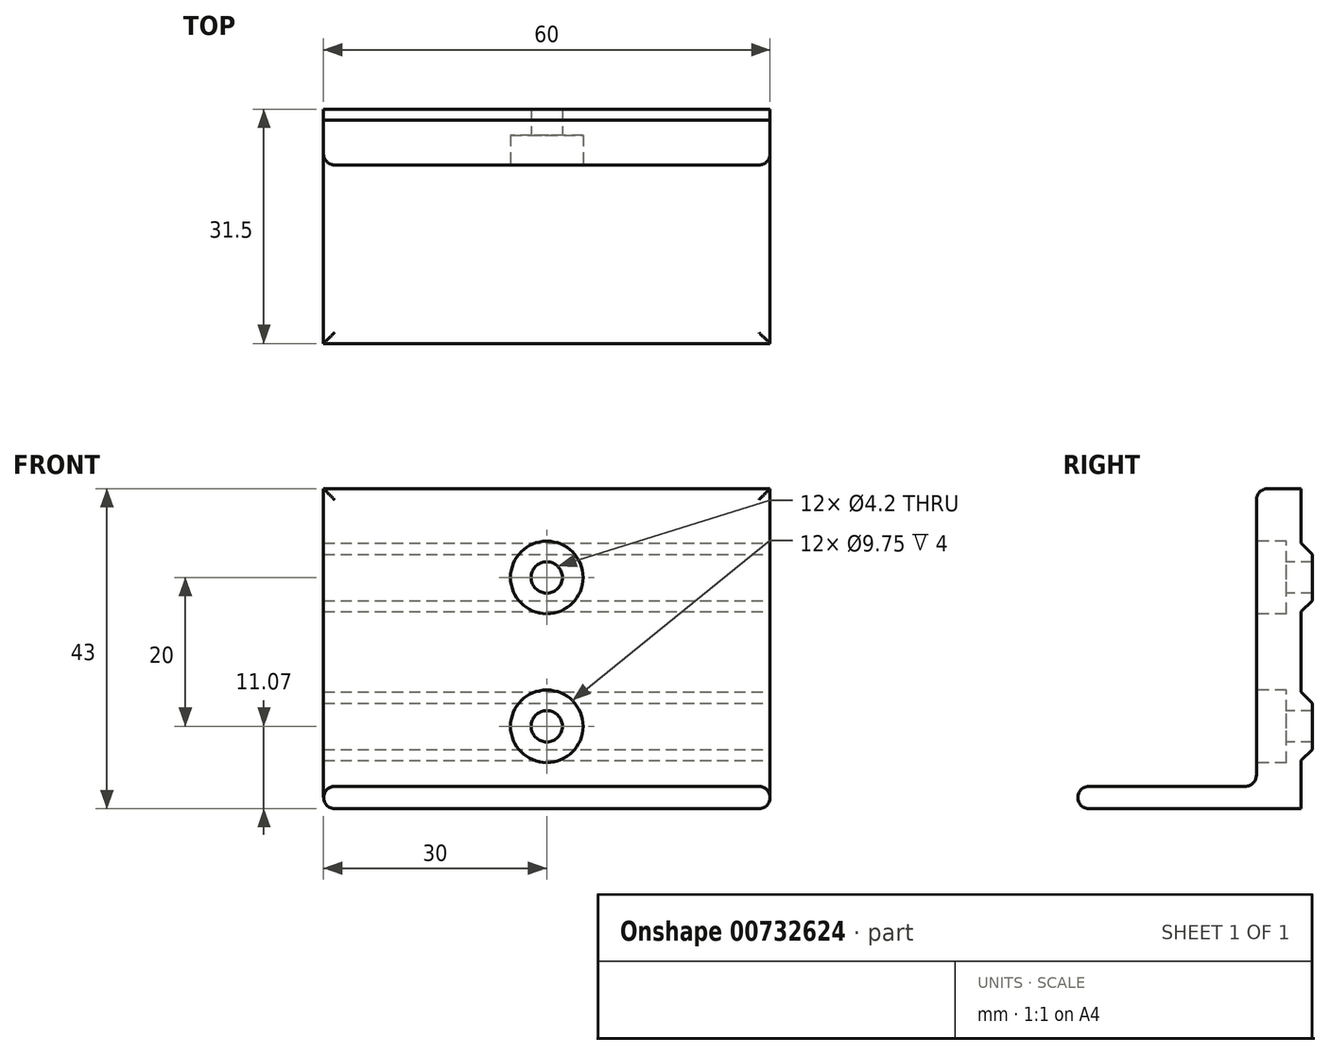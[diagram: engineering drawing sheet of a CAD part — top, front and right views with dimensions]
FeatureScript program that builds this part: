
annotation { "Feature Type Name" : "Feature", "Feature Type Description" : "" }
export const myFeature = defineFeature(function(context is Context, id is Id, definition is map)
    precondition{}
    {
        {
            var Q0;
            Q0=qCreatedBy(makeId("Right.planeOp"),FACE);
            var sketch = newSketch(context, id + "F0", { "sketchPlane" : qUnion([Q0])});
            skLineSegment(sketch, "E0.MirrorCS", {"start": v(4, 1.93) * mm, "end": v(10, 1.93) * mm});
            skLineSegment(sketch, "E1.MirrorCS", {"start": v(10, -5.4) * mm, "end": v(10, 1.93) * mm});
            skLineSegment(sketch, "E2.MirrorCS", {"start": v(11.5, -6.9) * mm, "end": v(10, -5.4) * mm});
            skLineSegment(sketch, "E3.MirrorCS", {"start": v(11.5, -33.1) * mm, "end": v(10, -34.6) * mm});
            skLineSegment(sketch, "E4.MirrorCS", {"start": v(11.5, -26.9) * mm, "end": v(10, -25.4) * mm});
            skLineSegment(sketch, "E5.MirrorCS", {"start": v(11.5, -13.1) * mm, "end": v(10, -14.6) * mm});
            skLineSegment(sketch, "E6.MirrorCS", {"start": v(11.5, -26.9) * mm, "end": v(11.5, -33.1) * mm});
            skLineSegment(sketch, "E7.MirrorCS", {"start": v(10, -14.6) * mm, "end": v(10, -25.4) * mm});
            skLineSegment(sketch, "E8.MirrorCS", {"start": v(11.5, -6.9) * mm, "end": v(11.5, -13.1) * mm});
            skLineSegment(sketch, "E9", {"start": v(4, 1.93) * mm, "end": v(4, -38.07) * mm});
            skLineSegment(sketch, "E10", {"start": v(10, -34.6) * mm, "end": v(10, -41.07) * mm});
            skLineSegment(sketch, "E11", {"start": v(10, -41.07) * mm, "end": v(-20, -41.07) * mm});
            skLineSegment(sketch, "E12", {"start": v(-20, -41.07) * mm, "end": v(-20, -38.07) * mm});
            skLineSegment(sketch, "E13", {"start": v(-20, -38.07) * mm, "end": v(4, -38.07) * mm});
            skSolve(sketch);
        }
        {
            var Q0;
            {var subQ0=sQuery(id+"F0.wireOp",EDGE,"E0.MirrorCS");Q0=makeQuery(id+"F0.imprint","IMPRINT",FACE,{"disambiguationData":[TD([[makeQuery(id+"F0.imprint","IMPRINT",EDGE,{"derivedFrom":subQ0}),-1.0]])]});}
            var Q1;
            {var subQ0=sQuery(id+"F0.wireOp",EDGE,"9rQqoNrq-cJOX-mU7k-ljHF-MaSHiNsMoPpL");Q1=makeQuery(id+"F0.imprint","IMPRINT",FACE,{"disambiguationData":[TD([[makeQuery(id+"F0.imprint","IMPRINT",EDGE,{"derivedFrom":subQ0}),-1.0]])]});}
            extrude(context, id + "F1", {"entities" : qUnion([Q0, Q1]), "oppositeDirection" : true, "depth" : 60 * mm, "offsetDistance" : 25 * mm});
        }
        {
            var Q0;
            Q0=makeQuery(id+"F1.opExtrude","CAP_EDGE",EDGE,{"disambiguationData":[OSD([sQuery(id+"F0.wireOp",EDGE,"E9")])],"isStart":true});
            var Q1;
            Q1=makeQuery(id+"F1.opExtrude","CAP_EDGE",EDGE,{"disambiguationData":[OSD([sQuery(id+"F0.wireOp",EDGE,"E9")])],"isStart":false});
            var Q2;
            Q2=makeQuery(id+"F1.opExtrude","CAP_EDGE",EDGE,{"disambiguationData":[OSD([sQuery(id+"F0.wireOp",EDGE,"E13")])],"isStart":true});
            var Q3;
            Q3=makeQuery(id+"F1.opExtrude","SWEPT_EDGE",EDGE,{"disambiguationData":[OSD([sQuery(id+"F0.wireOp",EDGE,"E12"),sQuery(id+"F0.wireOp",EDGE,"E13")])]});
            var Q4;
            Q4=makeQuery(id+"F1.opExtrude","CAP_EDGE",EDGE,{"disambiguationData":[OSD([sQuery(id+"F0.wireOp",EDGE,"E13")])],"isStart":false});
            var Q5;
            Q5=makeQuery(id+"F1.opExtrude","SWEPT_EDGE",EDGE,{"disambiguationData":[OSD([sQuery(id+"F0.wireOp",EDGE,"E9"),sQuery(id+"F0.wireOp",EDGE,"E13")])]});
            var Q6;
            Q6=makeQuery(id+"F1.opExtrude","SWEPT_EDGE",EDGE,{"disambiguationData":[OSD([sQuery(id+"F0.wireOp",EDGE,"E11"),sQuery(id+"F0.wireOp",EDGE,"E12")])]});
            var Q7;
            Q7=makeQuery(id+"F1.opExtrude","CAP_EDGE",EDGE,{"disambiguationData":[OSD([sQuery(id+"F0.wireOp",EDGE,"E11")])],"isStart":true});
            var Q8;
            Q8=makeQuery(id+"F1.opExtrude","CAP_EDGE",EDGE,{"disambiguationData":[OSD([sQuery(id+"F0.wireOp",EDGE,"E11")])],"isStart":false});
            var Q9;
            Q9=makeQuery(id+"F1.opExtrude","SWEPT_EDGE",EDGE,{"disambiguationData":[OSD([sQuery(id+"F0.wireOp",EDGE,"E0.MirrorCS"),sQuery(id+"F0.wireOp",EDGE,"E9")])]});
            fillet(context, id + "F2", {"entities" : qUnion([Q0, Q1, Q2, Q3, Q4, Q5, Q6, Q7, Q8, Q9]), "radius" : 1.5 * mm, "tangentPropagation" : true, "allowEdgeOverflow" : false});
        }
        {
            var Q0;
            Q0=makeQuery(id+"F1.opExtrude","SWEPT_FACE",FACE,{"disambiguationData":[OSD([sQuery(id+"F0.wireOp",EDGE,"E9")])]});
            var sketch = newSketch(context, id + "F3", { "sketchPlane" : qUnion([Q0])});
            skPoint(sketch, "E14", {"position": v(-30, -10) * mm});
            skPoint(sketch, "E14.positionSnap0", {"position": v(-30, 1.93) * mm});
            skPoint(sketch, "E15", {"position": v(-30, -30) * mm});
            skSolve(sketch);
        }
        {
            var Q0;
            Q0=sQuery(id+"F3.wireOp",VERTEX,"E14");
            var Q1;
            Q1=sQuery(id+"F3.wireOp",VERTEX,"E15");
            var Q2;
            Q2=makeQuery(id+"F1.opExtrude","SWEPT_BODY",BODY,{"disambiguationData":[OSD([sQuery(id+"F0.wireOp",EDGE,"E0.MirrorCS"),sQuery(id+"F0.wireOp",EDGE,"E1.MirrorCS"),sQuery(id+"F0.wireOp",EDGE,"E2.MirrorCS"),sQuery(id+"F0.wireOp",EDGE,"E3.MirrorCS"),sQuery(id+"F0.wireOp",EDGE,"E4.MirrorCS"),sQuery(id+"F0.wireOp",EDGE,"E5.MirrorCS"),sQuery(id+"F0.wireOp",EDGE,"E6.MirrorCS"),sQuery(id+"F0.wireOp",EDGE,"E7.MirrorCS"),sQuery(id+"F0.wireOp",EDGE,"E8.MirrorCS"),sQuery(id+"F0.wireOp",EDGE,"E9"),sQuery(id+"F0.wireOp",EDGE,"E10"),sQuery(id+"F0.wireOp",EDGE,"E11"),sQuery(id+"F0.wireOp",EDGE,"E12"),sQuery(id+"F0.wireOp",EDGE,"E13")])]});
            hole(context, id + "F4", {"style" : HoleStyle.C_BORE, "endStyle" : HoleEndStyle.THROUGH, "holeDiameter" : 4.2 * mm, "cBoreDiameter" : 9.75 * mm, "cBoreDepth" : 4 * mm, "majorDiameter" : 5 * mm, "isTappedThrough" : true, "tappedDepth" : 12 * mm, "tapClearance" : 3, "startFromSketch" : true, "locations" : qUnion([Q0, Q1]), "scope" : qUnion([Q2])});
        }
    });
